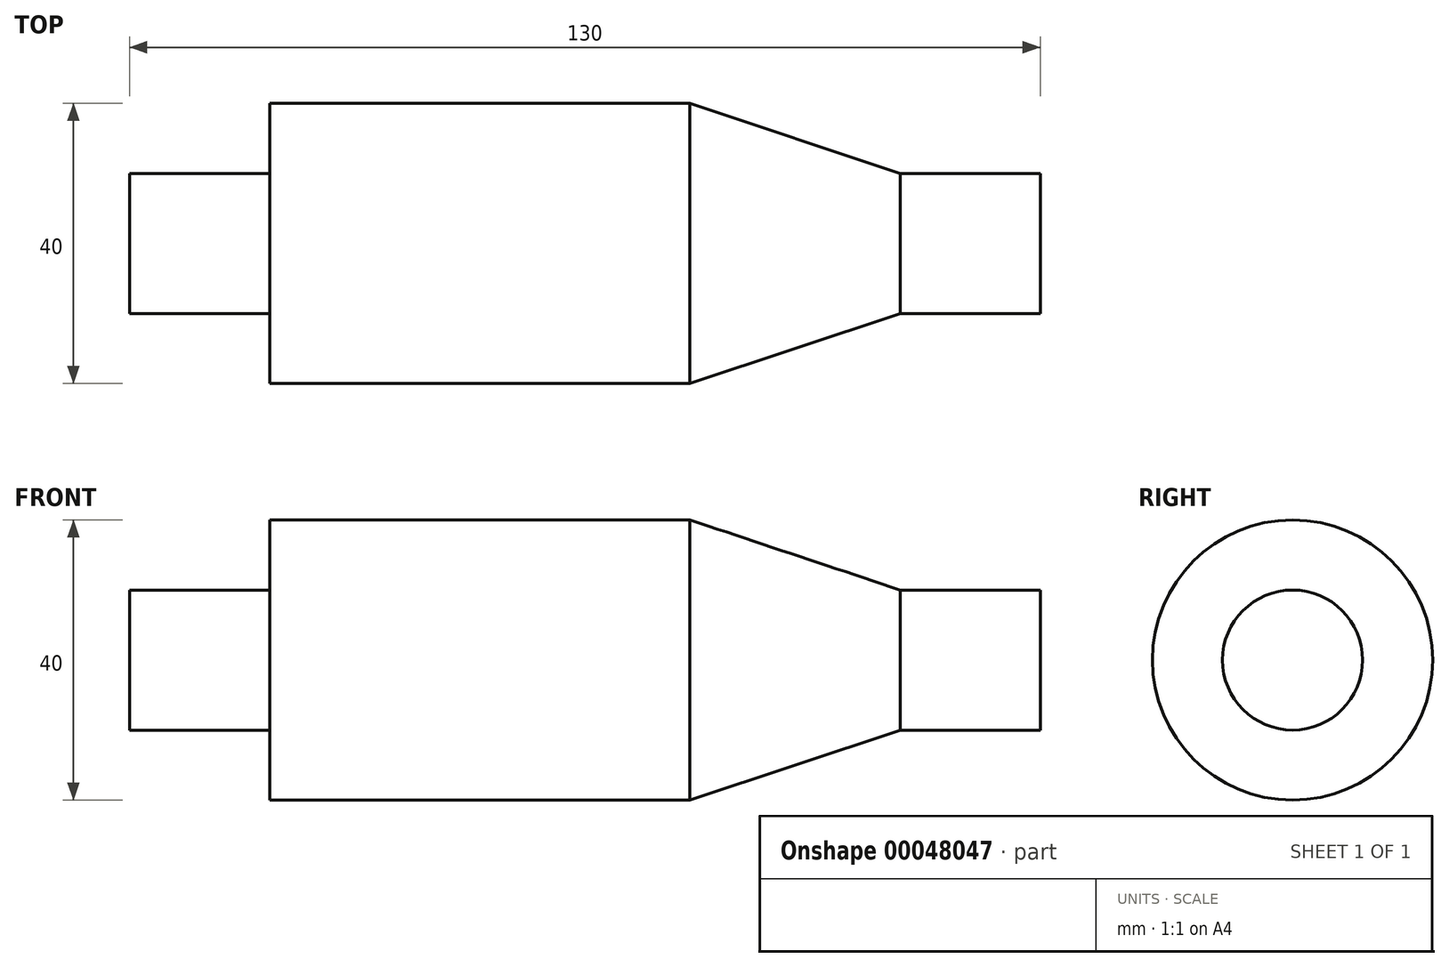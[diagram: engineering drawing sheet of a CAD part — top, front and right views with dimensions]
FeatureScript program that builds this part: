
annotation { "Feature Type Name" : "Feature", "Feature Type Description" : "" }
export const myFeature = defineFeature(function(context is Context, id is Id, definition is map)
    precondition{}
    {
        {
            var Q0;
            Q0=qCreatedBy(makeId("Front.planeOp"),FACE);
            var sketch = newSketch(context, id + "F0", { "sketchPlane" : qUnion([Q0])});
            skLineSegment(sketch, "E0", {"start": v(0, 0) * mm, "end": v(0, 10) * mm});
            skLineSegment(sketch, "E1", {"start": v(0, 10) * mm, "end": v(20, 10) * mm});
            skLineSegment(sketch, "E2", {"start": v(20, 10) * mm, "end": v(20, 20) * mm});
            skLineSegment(sketch, "E3", {"start": v(20, 20) * mm, "end": v(80, 20) * mm});
            skLineSegment(sketch, "E4", {"start": v(80, 20) * mm, "end": v(110, 10) * mm});
            skLineSegment(sketch, "E5", {"start": v(110, 10) * mm, "end": v(130, 10) * mm});
            skLineSegment(sketch, "E6", {"start": v(130, 10) * mm, "end": v(130, 0) * mm});
            skLineSegment(sketch, "E7", {"start": v(0, 0) * mm, "end": v(130, 0) * mm});
            skLineSegment(sketch, "E8", {"start": v(-63.57, 0) * mm, "end": v(175.4, 0) * mm, "construction": true});
            skSolve(sketch);
        }
        {
            var Q0;
            Q0=makeQuery(id+"F0.imprint","IMPRINT",FACE,{"disambiguationData":[TD([[makeQuery(id+"F0.imprint","IMPRINT",EDGE,{"derivedFrom":sQuery(id+"F0.wireOp",EDGE,"E0")}),-1.0]])]});
            var Q1;
            Q1=sQuery(id+"F0.wireOp",EDGE,"E8");
            revolve(context, id + "F1", {"entities" : qUnion([Q0]), "axis" : qUnion([Q1]), "revolveType" : RevolveType.FULL});
        }
    });
